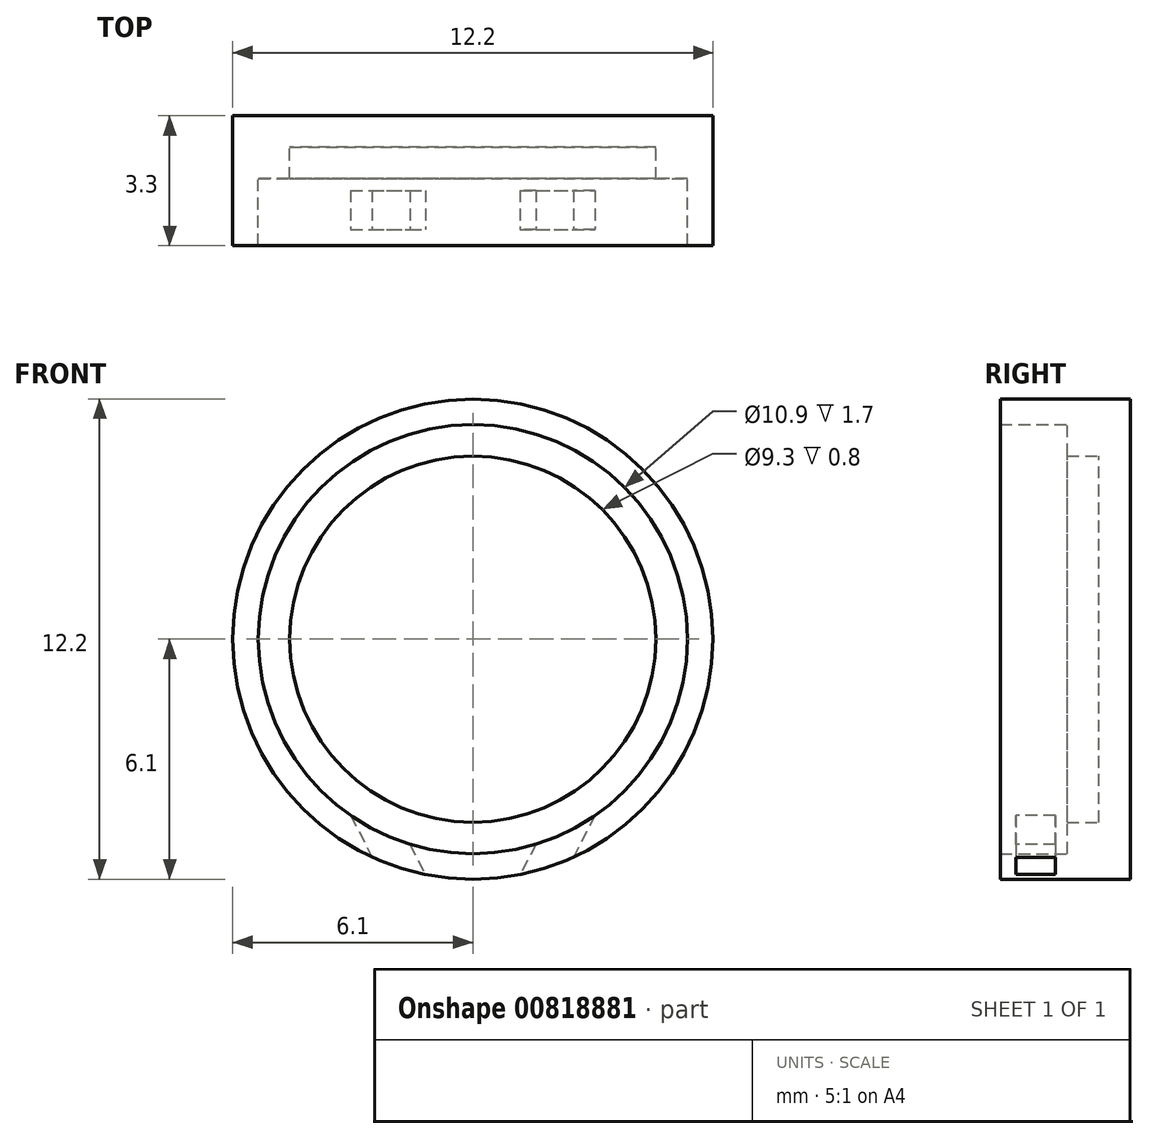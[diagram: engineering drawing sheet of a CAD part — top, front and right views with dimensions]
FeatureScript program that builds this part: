
annotation { "Feature Type Name" : "Feature", "Feature Type Description" : "" }
export const myFeature = defineFeature(function(context is Context, id is Id, definition is map)
    precondition{}
    {
        {
            var Q0;
            Q0=qCreatedBy(makeId("Front.planeOp"),FACE);
            var sketch = newSketch(context, id + "F0", { "sketchPlane" : qUnion([Q0])});
            skCircle(sketch, "E0", {"center": v(0, 0) * mm, "radius": 5 * mm});
            skCircle(sketch, "E1", {"center": v(0, 0) * mm, "radius": 6.1 * mm});
            skSolve(sketch);
        }
        {
            var Q0;
            Q0=makeQuery(id+"F0.imprint","IMPRINT",FACE,{"disambiguationData":[TD([[makeQuery(id+"F0.imprint","IMPRINT",EDGE,{"derivedFrom":sQuery(id+"F0.wireOp",EDGE,"E0")}),-1.0]])]});
            var Q1;
            Q1=makeQuery(id+"F0.imprint","IMPRINT",FACE,{"disambiguationData":[TD([[makeQuery(id+"F0.imprint","IMPRINT",EDGE,{"derivedFrom":sQuery(id+"F0.wireOp",EDGE,"E0")}),1.0]])]});
            extrude(context, id + "F1", {"entities" : qUnion([Q0, Q1]), "depth" : 0.8 * mm, "offsetDistance" : 25 * mm});
        }
        {
            var Q0;
            Q0=makeQuery(id+"F1.opExtrude","CAP_FACE",FACE,{"disambiguationData":[OSD([sQuery(id+"F0.wireOp",EDGE,"E1")])],"isStart":false});
            var sketch = newSketch(context, id + "F2", { "sketchPlane" : qUnion([Q0])});
            skCircle(sketch, "E2", {"center": v(0, 0) * mm, "radius": 5.45 * mm});
            skCircle(sketch, "E3", {"center": v(0, 0) * mm, "radius": 6.1 * mm});
            skSolve(sketch);
        }
        {
            var Q0;
            Q0=makeQuery(id+"F2.imprint","IMPRINT",FACE,{"disambiguationData":[TD([[makeQuery(id+"F2.imprint","IMPRINT",EDGE,{"derivedFrom":sQuery(id+"F2.wireOp",EDGE,"E2")}),-1.0]])]});
            extrude(context, id + "F3", {"entities" : qUnion([Q0]), "operationType" : NewBodyOperationType.ADD, "depth" : 2.5 * mm, "offsetDistance" : 25 * mm});
        }
        {
            var Q0;
            Q0=makeQuery(id+"F1.opExtrude","CAP_FACE",FACE,{"disambiguationData":[OSD([sQuery(id+"F0.wireOp",EDGE,"E1")])],"isStart":false});
            var sketch = newSketch(context, id + "F4", { "sketchPlane" : qUnion([Q0])});
            skCircle(sketch, "E4", {"center": v(0, 0) * mm, "radius": 4.65 * mm});
            skSolve(sketch);
        }
        {
            var Q0;
            Q0=makeQuery(id+"F4.imprint","IMPRINT",FACE,{"disambiguationData":[TD([[makeQuery(id+"F4.imprint","IMPRINT",EDGE,{"derivedFrom":sQuery(id+"F4.wireOp",EDGE,"E4")}),-1.0]])]});
            extrude(context, id + "F5", {"entities" : qUnion([Q0]), "operationType" : NewBodyOperationType.ADD, "depth" : 0.8 * mm, "offsetDistance" : 25 * mm});
        }
        {
            var Q0;
            Q0=makeQuery(id+"F3.opExtrude","CAP_FACE",FACE,{"disambiguationData":[OSD([sQuery(id+"F2.wireOp",EDGE,"E2"),sQuery(id+"F2.wireOp",EDGE,"E3")])],"isStart":false});
            var sketch = newSketch(context, id + "F6", { "sketchPlane" : qUnion([Q0])});
            skLineSegment(sketch, "E5", {"start": v(-1.6, -5.2) * mm, "end": v(-1.2, -5.98) * mm});
            skLineSegment(sketch, "E6", {"start": v(-3.1, -4.48) * mm, "end": v(-2.56, -5.54) * mm});
            skLineSegment(sketch, "E7.MirrorCS", {"start": v(1.6, -5.2) * mm, "end": v(1.2, -5.98) * mm});
            skLineSegment(sketch, "E8.MirrorCS", {"start": v(3.1, -4.48) * mm, "end": v(2.56, -5.54) * mm});
            skSolve(sketch);
        }
        {
            var Q0;
            {var subQ0=sQuery(id+"F6.wireOp",EDGE,"E5");Q0=makeQuery(id+"F6.imprint","IMPRINT",FACE,{"disambiguationData":[TD([[makeQuery(id+"F6.imprint","IMPRINT",EDGE,{"derivedFrom":subQ0}),-1.0]])]});}
            var Q1;
            {var subQ0=sQuery(id+"F6.wireOp",EDGE,"E7.MirrorCS");Q1=makeQuery(id+"F6.imprint","IMPRINT",FACE,{"disambiguationData":[TD([[makeQuery(id+"F6.imprint","IMPRINT",EDGE,{"derivedFrom":subQ0}),1.0]])]});}
            extrude(context, id + "F7", {"entities" : qUnion([Q0, Q1]), "operationType" : NewBodyOperationType.REMOVE, "oppositeDirection" : true, "depth" : 1.4 * mm, "offsetDistance" : 25 * mm});
        }
        {
            var Q0;
            {var subQ0=sQuery(id+"F2.wireOp",EDGE,"E3");var subQ1=sQuery(id+"F2.wireOp",EDGE,"E2");Q0=makeQuery(id+"F7.boolean.opBoolean","SPLIT",FACE,{"disambiguationData":[TD([makeQuery(id+"F7.opExtrude","SWEPT_FACE",FACE,{"disambiguationData":[OSD([sQuery(id+"F6.wireOp",EDGE,"E6")])]})])],"derivedFrom":makeQuery(id+"F3.opExtrude","CAP_FACE",FACE,{"disambiguationData":[OSD([subQ1,subQ0])],"isStart":false})});}
            var sketch = newSketch(context, id + "F8", { "sketchPlane" : qUnion([Q0])});
            skArc(sketch, "E9", {"start": v(-3.1, -4.48) * mm, "mid": v(-2.38, -4.9) * mm, "end": v(-1.6, -5.2) * mm});
            skArc(sketch, "E10", {"start": v(-2.56, -5.54) * mm, "mid": v(-1.9, -5.8) * mm, "end": v(-1.2, -5.98) * mm});
            skLineSegment(sketch, "E11", {"start": v(-3.1, -4.48) * mm, "end": v(-2.56, -5.54) * mm});
            skLineSegment(sketch, "E12", {"start": v(-1.6, -5.2) * mm, "end": v(-1.2, -5.98) * mm});
            skLineSegment(sketch, "E13.MirrorCS", {"start": v(3.1, -4.48) * mm, "end": v(2.56, -5.54) * mm});
            skArc(sketch, "E14.MirrorCS", {"start": v(2.56, -5.54) * mm, "mid": v(1.9, -5.8) * mm, "end": v(1.2, -5.98) * mm});
            skLineSegment(sketch, "E15.MirrorCS", {"start": v(1.6, -5.2) * mm, "end": v(1.2, -5.98) * mm});
            skArc(sketch, "E16.MirrorCS", {"start": v(3.1, -4.48) * mm, "mid": v(2.38, -4.9) * mm, "end": v(1.6, -5.2) * mm});
            skSolve(sketch);
        }
        {
            var Q0;
            Q0=makeQuery(id+"F8.imprint","IMPRINT",FACE,{"disambiguationData":[TD([[makeQuery(id+"F8.imprint","IMPRINT",EDGE,{"derivedFrom":sQuery(id+"F8.wireOp",EDGE,"E9")}),-1.0]])]});
            var Q1;
            Q1=makeQuery(id+"F8.imprint","IMPRINT",FACE,{"disambiguationData":[TD([[makeQuery(id+"F8.imprint","IMPRINT",EDGE,{"derivedFrom":sQuery(id+"F8.wireOp",EDGE,"E13.MirrorCS")}),-1.0]])]});
            extrude(context, id + "F9", {"entities" : qUnion([Q0, Q1]), "operationType" : NewBodyOperationType.ADD, "oppositeDirection" : true, "depth" : 0.4 * mm, "offsetDistance" : 25 * mm});
        }
    });
